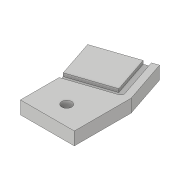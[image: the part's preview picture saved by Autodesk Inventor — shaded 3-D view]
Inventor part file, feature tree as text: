
AUTODESK INVENTOR PART (.ipt)
format: ipt  version: 2018.3 (Build 223284000, 284)  size: 109,056 bytes
history: native  units: in
note: dims shown in document units (in); Inventor stores cm internally (conversion verified against a paired STEP export)
features: extrude x2, sketch x2, fillet x1
ambient origin geometry x8: Origin, YZ Plane, XZ Plane, XY Plane, X Axis, Y Axis, Z Axis, Center Point
bodies: Solid1 (feature_tree)
feature tree (5):
  extrude  "Extrusion1"  Depth=0.25in TaperAngle=0.0deg
  extrude  "Extrusion2"  Depth=0.126in
  fillet  "Fillet1"  Radius=0.126in
  sketch  "Sketch1"  dims[d0=0.75in d1=0.875in d2=1.1003in d3=1.0432in d4=0.1925in d5=0.25in d6=0.0in]
  sketch  "Sketch2"  dims[d10=0.125in d11=0.126in d12=0.126in d13=0.0625in d14=0.0in d15=0.0in d16=0.0625in]
